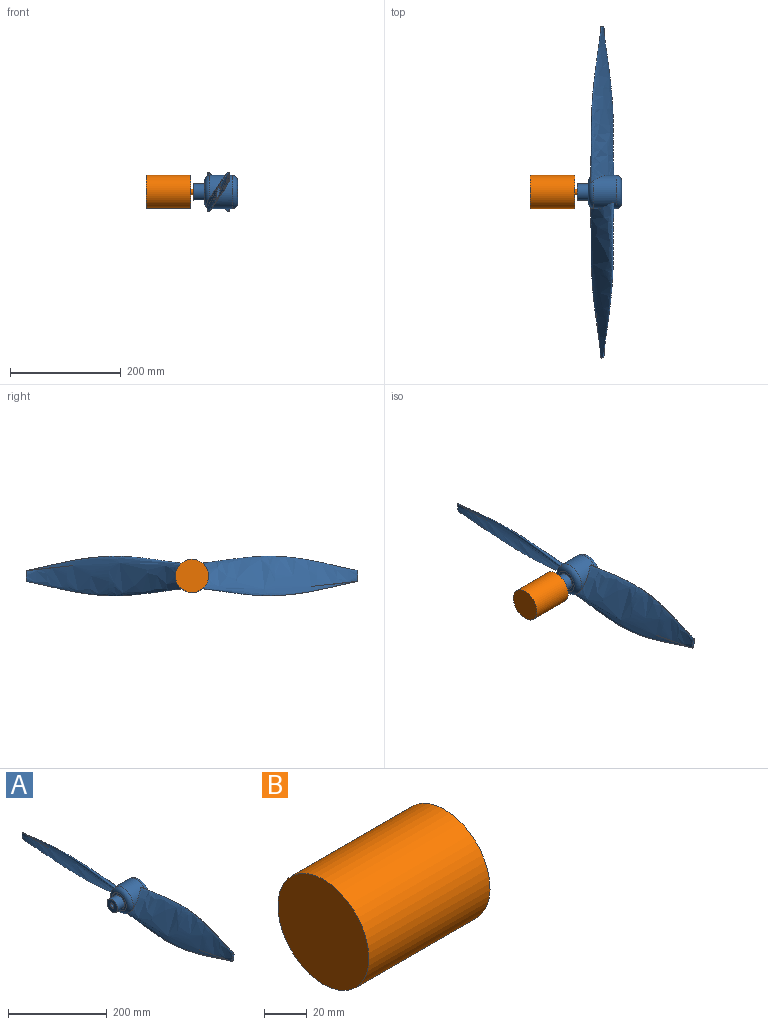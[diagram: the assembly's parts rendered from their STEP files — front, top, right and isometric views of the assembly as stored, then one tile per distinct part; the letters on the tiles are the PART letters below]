
ASSEMBLY  parts=2 mates=1
PART A: 16 faces, bbox 80x600x95 mm
  f0: plane 30x30mm, normal (-1,0,0), area 624.3mm2, adj f6,f11,f12,f13,f14
  f1: bspline ~300x95.03mm, area 35744.8mm2, adj f2,f4,f10
  f2: plane 19.74x6.03mm, normal (0,-1,0), area 78.5mm2, adj f1
  f3: plane 40x40mm, normal (1,0,0), area 1256.6mm2, adj f9
  f4: cylinder r=30mm len=60mm, axis (-1,0,0), area 6317.7mm2, adj f1,f8,f9,f10
  f5: plane 40x40mm, normal (-1,0,0), area 549.8mm2, adj f6,f10
  f6: cylinder r=15mm len=30mm, axis (-1,0,0), area 1885mm2, adj f0,f5
  f7: plane 19.74x6.03mm, normal (0,1,0), area 78.5mm2, adj f8
  f8: bspline ~300x95.03mm, area 35744.8mm2, adj f4,f7,f10
  f9: torus R=20mm, axis (-1,0,0), area 2602.2mm2, adj f3,f4
  f10: torus R=20mm, axis (1,0,0), area 2470.8mm2, adj f1,f4,f5,f8
  f11: plane 10x2mm, normal (0,0,-1), area 20mm2, adj f0,f12,f14,f15
  f12: plane 10x2.1mm, normal (0,-1,0), area 21mm2, adj f0,f11,f13,f15
  f13: cylinder r=5mm len=10mm, axis (-1,0,0), area 294mm2, adj f0,f12,f14,f15
  f14: plane 10x2.1mm, normal (0,1,0), area 21mm2, adj f0,f11,f13,f15
  f15: plane 12x10mm, normal (-1,0,0), area 82.6mm2, adj f11,f12,f13,f14
PART B: 5 faces, bbox 95x60x60 mm
  f0: plane 60x60mm, normal (-1,0,0), area 2827.4mm2, adj f4
  f1: plane 10x10mm, normal (1,0,0), area 78.5mm2, adj f2
  f2: cylinder r=5mm len=15mm, axis (-1,0,0), area 471.2mm2, adj f1,f3
  f3: plane 60x60mm, normal (1,0,0), area 2748.9mm2, adj f2,f4
  f4: cylinder r=30mm len=80mm, axis (-1,0,0), area 15079.6mm2, adj f0,f3
PLACE A t=(-150.22,55.27,-23.07)mm
PLACE B t=(-229.82,55.27,-22.78)mm
MATE revolute A.f15 <-> B.f2  axis (-1,0,0) through (-185.22,55.27,-22.78)mm
